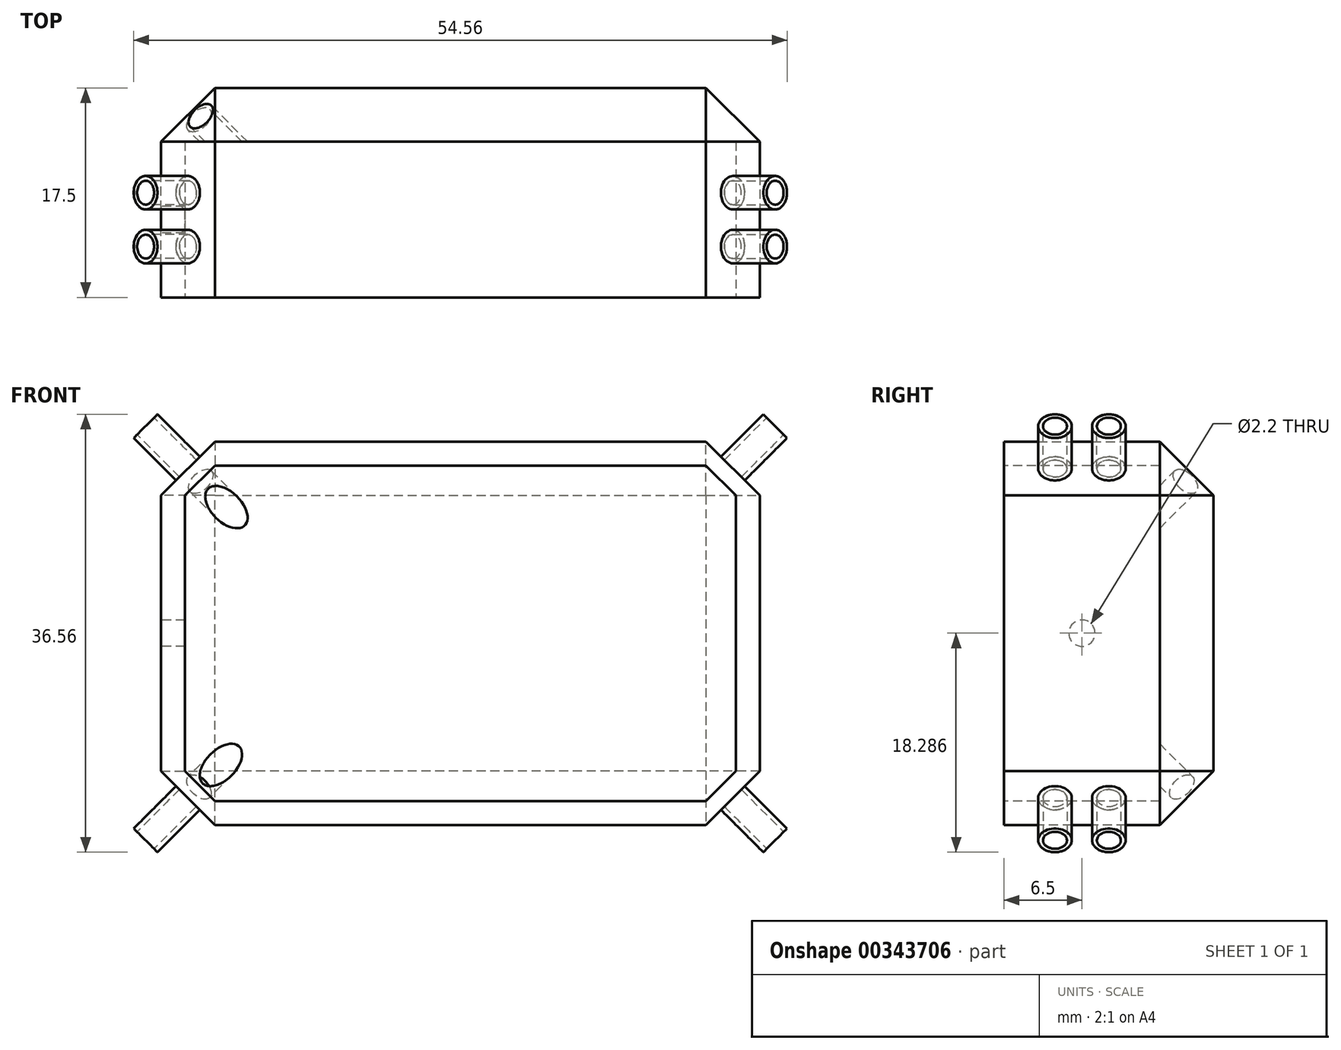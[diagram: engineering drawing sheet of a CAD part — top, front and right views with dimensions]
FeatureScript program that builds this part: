
annotation { "Feature Type Name" : "Feature", "Feature Type Description" : "" }
export const myFeature = defineFeature(function(context is Context, id is Id, definition is map)
    precondition{}
    {
        {
            var Q0;
            Q0=qCreatedBy(makeId("Front.planeOp"),FACE);
            var sketch = newSketch(context, id + "F0", { "sketchPlane" : qUnion([Q0])});
            skLineSegment(sketch, "E0.bottom", {"start": v(0, 0) * mm, "end": v(50, 0) * mm});
            skLineSegment(sketch, "E0.top", {"start": v(0, 32) * mm, "end": v(50, 32) * mm});
            skLineSegment(sketch, "E0.left", {"start": v(0, 0) * mm, "end": v(0, 32) * mm});
            skLineSegment(sketch, "E0.right", {"start": v(50, 0) * mm, "end": v(50, 32) * mm});
            skSolve(sketch);
        }
        {
            var Q0;
            Q0 = qSketchRegion(id + "F0", true);
            extrude(context, id + "F1", {"entities" : qUnion([Q0]), "depth" : 24 * mm, "offsetDistance" : 25.4 * mm});
        }
        {
            var Q0;
            Q0=makeQuery(id+"F1.opExtrude","SWEPT_FACE",FACE,{"disambiguationData":[OSD([sQuery(id+"F0.wireOp",EDGE,"E0.right")])]});
            var Q1;
            Q1=makeQuery(id+"F1.opExtrude","SWEPT_FACE",FACE,{"disambiguationData":[OSD([sQuery(id+"F0.wireOp",EDGE,"E0.top")])]});
            var Q2;
            Q2=makeQuery(id+"F1.opExtrude","SWEPT_FACE",FACE,{"disambiguationData":[OSD([sQuery(id+"F0.wireOp",EDGE,"E0.left")])]});
            var Q3;
            Q3=makeQuery(id+"F1.opExtrude","SWEPT_FACE",FACE,{"disambiguationData":[OSD([sQuery(id+"F0.wireOp",EDGE,"E0.bottom")])]});
            chamfer(context, id + "F2", {"entities" : qUnion([Q0, Q1, Q2, Q3]), "width" : 4.5 * mm, "tangentPropagation" : true});
        }
        {
            var Q0;
            Q0=makeQuery(id+"F1.opExtrude","CAP_FACE",FACE,{"disambiguationData":[OSD([sQuery(id+"F0.wireOp",EDGE,"E0.bottom"),sQuery(id+"F0.wireOp",EDGE,"E0.top"),sQuery(id+"F0.wireOp",EDGE,"E0.left"),sQuery(id+"F0.wireOp",EDGE,"E0.right")])],"isStart":false});
            var sketch = newSketch(context, id + "F3", { "sketchPlane" : qUnion([Q0])});
            skLineSegment(sketch, "E1.bottom", {"start": v(55.01, 52.4) * mm, "end": v(-9.6, 52.4) * mm});
            skLineSegment(sketch, "E1.top", {"start": v(55.01, -20.26) * mm, "end": v(-9.6, -20.26) * mm});
            skLineSegment(sketch, "E1.left", {"start": v(55.01, 52.4) * mm, "end": v(55.01, -20.26) * mm});
            skLineSegment(sketch, "E1.right", {"start": v(-9.6, 52.4) * mm, "end": v(-9.6, -20.26) * mm});
            skSolve(sketch);
        }
        {
            var Q0;
            Q0 = qSketchRegion(id + "F3", true);
            extrude(context, id + "F4", {"entities" : qUnion([Q0]), "operationType" : NewBodyOperationType.REMOVE, "oppositeDirection" : true, "depth" : 6.5 * mm, "offsetDistance" : 25.4 * mm});
        }
        {
            var Q0;
            Q0=makeQuery(id+"F4.boolean.opBoolean","COPY",FACE,{"derivedFrom":makeQuery(id+"F4.opExtrude","CAP_FACE",FACE,{"disambiguationData":[OSD([sQuery(id+"F3.wireOp",EDGE,"E1.bottom"),sQuery(id+"F3.wireOp",EDGE,"E1.top"),sQuery(id+"F3.wireOp",EDGE,"E1.left"),sQuery(id+"F3.wireOp",EDGE,"E1.right")])],"isStart":false})});
            var sketch = newSketch(context, id + "F5", { "sketchPlane" : qUnion([Q0])});
            skLineSegment(sketch, "E2", {"start": v(2, 27.5) * mm, "end": v(2, 4.5) * mm});
            skLineSegment(sketch, "E3", {"start": v(2, 27.5) * mm, "end": v(4.5, 30) * mm});
            skLineSegment(sketch, "E4", {"start": v(4.5, 30) * mm, "end": v(45.5, 30) * mm});
            skLineSegment(sketch, "E5", {"start": v(45.5, 30) * mm, "end": v(48, 27.5) * mm});
            skLineSegment(sketch, "E6", {"start": v(48, 27.5) * mm, "end": v(48, 4.5) * mm});
            skLineSegment(sketch, "E7", {"start": v(48, 4.5) * mm, "end": v(45.5, 2) * mm});
            skLineSegment(sketch, "E8", {"start": v(45.5, 2) * mm, "end": v(4.5, 2) * mm});
            skLineSegment(sketch, "E9", {"start": v(4.5, 2) * mm, "end": v(2, 4.5) * mm});
            skSolve(sketch);
        }
        {
            var Q0;
            Q0 = qSketchRegion(id + "F5", true);
            extrude(context, id + "F6", {"entities" : qUnion([Q0]), "operationType" : NewBodyOperationType.REMOVE, "oppositeDirection" : true, "depth" : 13 * mm, "offsetDistance" : 25.4 * mm});
        }
        {
            var Q0;
            {var subQ0=sQuery(id+"F0.wireOp",EDGE,"E0.right");var subQ1=sQuery(id+"F0.wireOp",EDGE,"E0.top");Q0=makeQuery(id+"F2.opChamfer","BLEND_FACE",FACE,{"disambiguationData":[OSD([subQ1,subQ0]),TDD([makeQuery(id+"F1.opExtrude","SWEPT_EDGE",EDGE,{"disambiguationData":[OSD([subQ1,subQ0])]})])]});}
            var sketch = newSketch(context, id + "F7", { "sketchPlane" : qUnion([Q0])});
            skCircle(sketch, "E10", {"center": v(-13.25, -12.73) * mm, "radius": 1.4 * mm});
            skPoint(sketch, "E10.centerSnap0", {"position": v(-17.5, -12.73) * mm});
            skCircle(sketch, "E11", {"center": v(-8.75, -12.73) * mm, "radius": 1.4 * mm});
            skSolve(sketch);
        }
        {
            var Q0;
            Q0 = qSketchRegion(id + "F7", true);
            extrude(context, id + "F8", {"entities" : qUnion([Q0]), "operationType" : NewBodyOperationType.ADD, "depth" : 5 * mm, "offsetDistance" : 25.4 * mm});
        }
        {
            var Q0;
            {var subQ0=sQuery(id+"F0.wireOp",EDGE,"E0.right");var subQ1=sQuery(id+"F0.wireOp",EDGE,"E0.bottom");Q0=makeQuery(id+"F2.opChamfer","BLEND_FACE",FACE,{"disambiguationData":[OSD([subQ1,subQ0]),TDD([makeQuery(id+"F1.opExtrude","SWEPT_EDGE",EDGE,{"disambiguationData":[OSD([subQ1,subQ0])]})])]});}
            var sketch = newSketch(context, id + "F9", { "sketchPlane" : qUnion([Q0])});
            skCircle(sketch, "E12", {"center": v(-13.25, 35.36) * mm, "radius": 1.4 * mm});
            skPoint(sketch, "E12.centerSnap0", {"position": v(-17.5, 35.36) * mm});
            skCircle(sketch, "E13", {"center": v(-8.75, 35.36) * mm, "radius": 1.4 * mm});
            skSolve(sketch);
        }
        {
            var Q0;
            Q0 = qSketchRegion(id + "F9", true);
            extrude(context, id + "F10", {"entities" : qUnion([Q0]), "operationType" : NewBodyOperationType.ADD, "depth" : 5 * mm, "offsetDistance" : 25.4 * mm});
        }
        {
            var Q0;
            {var subQ0=sQuery(id+"F0.wireOp",EDGE,"E0.left");var subQ1=sQuery(id+"F0.wireOp",EDGE,"E0.bottom");Q0=makeQuery(id+"F2.opChamfer","BLEND_FACE",FACE,{"disambiguationData":[OSD([subQ1,subQ0]),TDD([makeQuery(id+"F1.opExtrude","SWEPT_EDGE",EDGE,{"disambiguationData":[OSD([subQ1,subQ0])]})])]});}
            var sketch = newSketch(context, id + "F11", { "sketchPlane" : qUnion([Q0])});
            skCircle(sketch, "E14", {"center": v(13.25, 0) * mm, "radius": 1.4 * mm});
            skPoint(sketch, "E14.centerSnap0", {"position": v(17.5, 0) * mm});
            skCircle(sketch, "E15", {"center": v(8.75, 0) * mm, "radius": 1.4 * mm});
            skPoint(sketch, "E15.centerSnap0", {"position": v(4.5, 0) * mm});
            skSolve(sketch);
        }
        {
            var Q0;
            Q0 = qSketchRegion(id + "F11", true);
            extrude(context, id + "F12", {"entities" : qUnion([Q0]), "operationType" : NewBodyOperationType.ADD, "depth" : 5 * mm, "offsetDistance" : 25.4 * mm});
        }
        {
            var Q0;
            {var subQ0=sQuery(id+"F0.wireOp",EDGE,"E0.left");var subQ1=sQuery(id+"F0.wireOp",EDGE,"E0.top");Q0=makeQuery(id+"F2.opChamfer","BLEND_FACE",FACE,{"disambiguationData":[OSD([subQ1,subQ0]),TDD([makeQuery(id+"F1.opExtrude","SWEPT_EDGE",EDGE,{"disambiguationData":[OSD([subQ1,subQ0])]})])]});}
            var sketch = newSketch(context, id + "F13", { "sketchPlane" : qUnion([Q0])});
            skCircle(sketch, "E16", {"center": v(8.75, 22.63) * mm, "radius": 1.4 * mm});
            skPoint(sketch, "E16.centerSnap0", {"position": v(17.5, 22.63) * mm});
            skCircle(sketch, "E17", {"center": v(13.25, 22.63) * mm, "radius": 1.4 * mm});
            skSolve(sketch);
        }
        {
            var Q0;
            Q0 = qSketchRegion(id + "F13", true);
            extrude(context, id + "F14", {"entities" : qUnion([Q0]), "operationType" : NewBodyOperationType.ADD, "depth" : 5 * mm, "offsetDistance" : 25.4 * mm});
        }
        {
            var Q0;
            Q0=makeQuery(id+"F8.opExtrude","CAP_FACE",FACE,{"disambiguationData":[OSD([sQuery(id+"F7.wireOp",EDGE,"E10")])],"isStart":false});
            var sketch = newSketch(context, id + "F15", { "sketchPlane" : qUnion([Q0])});
            skCircle(sketch, "E18", {"center": v(-13.25, -12.73) * mm, "radius": 1 * mm});
            skCircle(sketch, "E19", {"center": v(-8.75, -12.73) * mm, "radius": 1 * mm});
            skSolve(sketch);
        }
        {
            var Q0;
            Q0 = qSketchRegion(id + "F15", true);
            var Q1;
            Q1 = qSketchRegion(id + "F17", true);
            extrude(context, id + "F16", {"entities" : qUnion([Q0, Q1]), "operationType" : NewBodyOperationType.REMOVE, "oppositeDirection" : true, "depth" : 5 * mm, "offsetDistance" : 25.4 * mm});
        }
        {
            var Q0;
            Q0=makeQuery(id+"F10.opExtrude","CAP_FACE",FACE,{"disambiguationData":[OSD([sQuery(id+"F9.wireOp",EDGE,"E12")])],"isStart":false});
            var sketch = newSketch(context, id + "F17", { "sketchPlane" : qUnion([Q0])});
            skCircle(sketch, "E20", {"center": v(-13.25, 35.36) * mm, "radius": 1 * mm});
            skCircle(sketch, "E21", {"center": v(-8.75, 35.36) * mm, "radius": 1 * mm});
            skSolve(sketch);
        }
        {
            var Q0;
            Q0 = qSketchRegion(id + "F17", true);
            extrude(context, id + "F18", {"entities" : qUnion([Q0]), "operationType" : NewBodyOperationType.REMOVE, "oppositeDirection" : true, "depth" : 5 * mm, "offsetDistance" : 25.4 * mm});
        }
        {
            var Q0;
            Q0=makeQuery(id+"F12.opExtrude","CAP_FACE",FACE,{"disambiguationData":[OSD([sQuery(id+"F11.wireOp",EDGE,"E14")])],"isStart":false});
            var sketch = newSketch(context, id + "F19", { "sketchPlane" : qUnion([Q0])});
            skCircle(sketch, "E22", {"center": v(13.25, 0) * mm, "radius": 1 * mm});
            skCircle(sketch, "E23", {"center": v(8.75, 0) * mm, "radius": 1 * mm});
            skSolve(sketch);
        }
        {
            var Q0;
            Q0 = qSketchRegion(id + "F19", true);
            extrude(context, id + "F20", {"entities" : qUnion([Q0]), "operationType" : NewBodyOperationType.REMOVE, "oppositeDirection" : true, "depth" : 5 * mm, "offsetDistance" : 25.4 * mm});
        }
        {
            var Q0;
            Q0=makeQuery(id+"F14.opExtrude","CAP_FACE",FACE,{"disambiguationData":[OSD([sQuery(id+"F13.wireOp",EDGE,"E16")])],"isStart":false});
            var sketch = newSketch(context, id + "F21", { "sketchPlane" : qUnion([Q0])});
            skCircle(sketch, "E24", {"center": v(8.75, 22.63) * mm, "radius": 1 * mm});
            skCircle(sketch, "E25", {"center": v(13.25, 22.63) * mm, "radius": 1 * mm});
            skSolve(sketch);
        }
        {
            var Q0;
            Q0 = qSketchRegion(id + "F21", true);
            extrude(context, id + "F22", {"entities" : qUnion([Q0]), "operationType" : NewBodyOperationType.REMOVE, "oppositeDirection" : true, "depth" : 5 * mm, "offsetDistance" : 25.4 * mm});
        }
        {
            var Q0;
            Q0=makeQuery(id+"F1.opExtrude","SWEPT_FACE",FACE,{"disambiguationData":[OSD([sQuery(id+"F0.wireOp",EDGE,"E0.left")])]});
            var sketch = newSketch(context, id + "F23", { "sketchPlane" : qUnion([Q0])});
            skCircle(sketch, "E26", {"center": v(11, 16) * mm, "radius": 1.1 * mm});
            skPoint(sketch, "E26.centerSnap0", {"position": v(11, 27.5) * mm});
            skSolve(sketch);
        }
        {
            var Q0;
            Q0 = qSketchRegion(id + "F23", true);
            extrude(context, id + "F24", {"entities" : qUnion([Q0]), "operationType" : NewBodyOperationType.REMOVE, "oppositeDirection" : true, "depth" : 25.4 * mm, "offsetDistance" : 25.4 * mm});
        }
        {
            var Q0;
            {var subQ0=sQuery(id+"F0.wireOp",EDGE,"E0.right");var subQ1=sQuery(id+"F0.wireOp",EDGE,"E0.top");Q0=makeQuery(id+"F2.opChamfer","BLEND_FACE",FACE,{"disambiguationData":[OSD([subQ1,subQ0]),TDD([makeQuery(id+"F1.opExtrude","CAP_VERTEX",VERTEX,{"disambiguationData":[OSD([subQ1,subQ0])],"isStart":true})])]});}
            var sketch = newSketch(context, id + "F25", { "sketchPlane" : qUnion([Q0])});
            skCircle(sketch, "E27", {"center": v(-33.06, -12.73) * mm, "radius": 1.25 * mm});
            skSolve(sketch);
        }
        {
            var Q0;
            Q0 = qSketchRegion(id + "F25", true);
            extrude(context, id + "F26", {"entities" : qUnion([Q0]), "operationType" : NewBodyOperationType.REMOVE, "oppositeDirection" : true, "depth" : 25.4 * mm, "offsetDistance" : 25.4 * mm});
        }
        {
            var Q0;
            {var subQ0=sQuery(id+"F0.wireOp",EDGE,"E0.right");var subQ1=sQuery(id+"F0.wireOp",EDGE,"E0.bottom");Q0=makeQuery(id+"F2.opChamfer","BLEND_FACE",FACE,{"disambiguationData":[OSD([subQ1,subQ0]),TDD([makeQuery(id+"F1.opExtrude","CAP_VERTEX",VERTEX,{"disambiguationData":[OSD([subQ1,subQ0])],"isStart":true})])]});}
            var sketch = newSketch(context, id + "F27", { "sketchPlane" : qUnion([Q0])});
            skCircle(sketch, "E28", {"center": v(-19.75, 35.36) * mm, "radius": 1.25 * mm});
            skSolve(sketch);
        }
        {
            var Q0;
            Q0 = qSketchRegion(id + "F27", true);
            extrude(context, id + "F28", {"entities" : qUnion([Q0]), "operationType" : NewBodyOperationType.REMOVE, "oppositeDirection" : true, "depth" : 25.4 * mm, "offsetDistance" : 25.4 * mm});
        }
        {
            var Q0;
            {var subQ0=sQuery(id+"F0.wireOp",EDGE,"E0.left");var subQ1=sQuery(id+"F0.wireOp",EDGE,"E0.top");Q0=makeQuery(id+"F2.opChamfer","BLEND_FACE",FACE,{"disambiguationData":[OSD([subQ1,subQ0]),TDD([makeQuery(id+"F1.opExtrude","CAP_VERTEX",VERTEX,{"disambiguationData":[OSD([subQ1,subQ0])],"isStart":true})])]});}
            var sketch = newSketch(context, id + "F29", { "sketchPlane" : qUnion([Q0])});
            skLineSegment(sketch, "E29", {"start": v(-14.9, 19.45) * mm, "end": v(-12.15, 24.22) * mm});
            skCircle(sketch, "E30", {"center": v(-13.46, 21.94) * mm, "radius": 1.25 * mm});
            skSolve(sketch);
        }
        {
            var Q0;
            Q0 = qSketchRegion(id + "F29", true);
            extrude(context, id + "F30", {"entities" : qUnion([Q0]), "operationType" : NewBodyOperationType.REMOVE, "oppositeDirection" : true, "depth" : 25.4 * mm, "offsetDistance" : 25.4 * mm});
        }
        {
            var Q0;
            {var subQ0=sQuery(id+"F0.wireOp",EDGE,"E0.left");var subQ1=sQuery(id+"F0.wireOp",EDGE,"E0.bottom");Q0=makeQuery(id+"F2.opChamfer","BLEND_FACE",FACE,{"disambiguationData":[OSD([subQ1,subQ0]),TDD([makeQuery(id+"F1.opExtrude","CAP_VERTEX",VERTEX,{"disambiguationData":[OSD([subQ1,subQ0])],"isStart":true})])]});}
            var sketch = newSketch(context, id + "F31", { "sketchPlane" : qUnion([Q0])});
            skLineSegment(sketch, "E31", {"start": v(-1.84, 3.18) * mm, "end": v(0.92, -1.6) * mm});
            skCircle(sketch, "E32", {"center": v(-0.2, 0.36) * mm, "radius": 1.25 * mm});
            skSolve(sketch);
        }
        {
            var Q0;
            Q0 = qSketchRegion(id + "F31", true);
            extrude(context, id + "F32", {"entities" : qUnion([Q0]), "operationType" : NewBodyOperationType.REMOVE, "oppositeDirection" : true, "depth" : 25.4 * mm, "offsetDistance" : 25.4 * mm});
        }
    });
